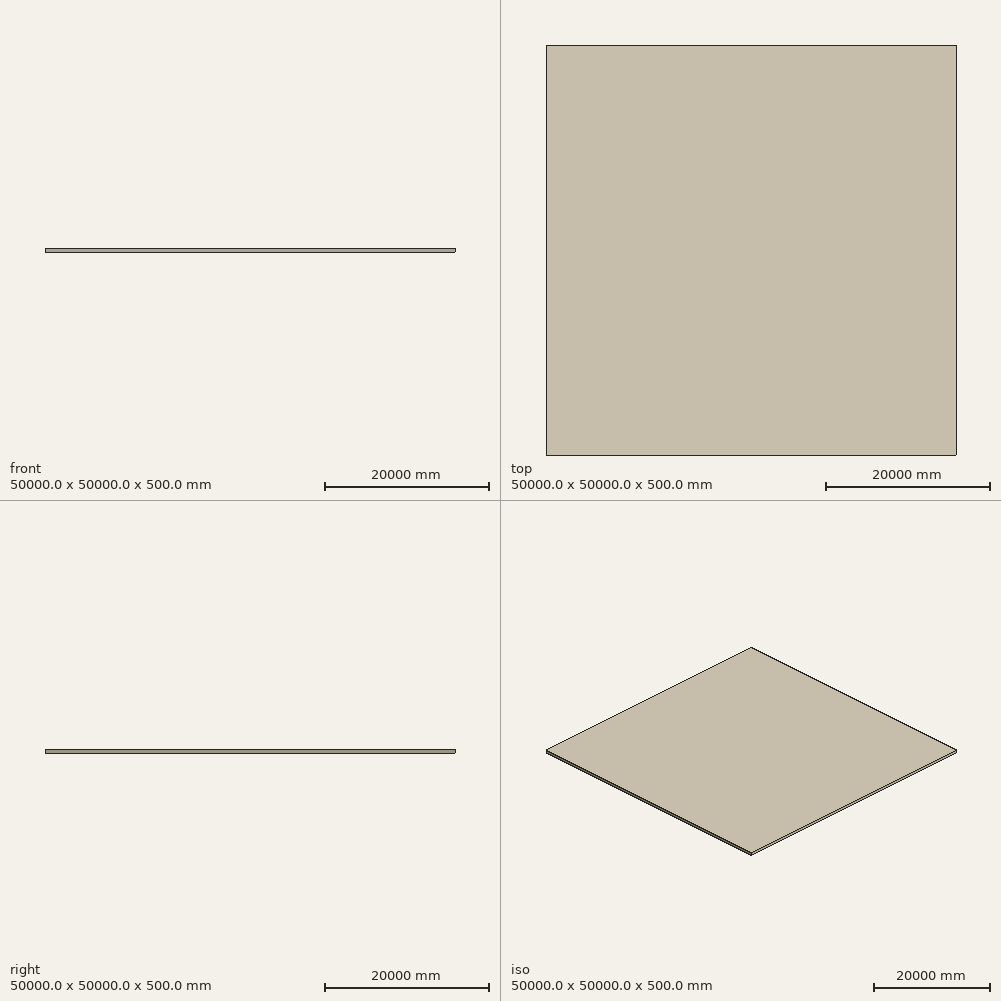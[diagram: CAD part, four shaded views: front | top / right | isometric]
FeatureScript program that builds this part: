
annotation { "Feature Type Name" : "Feature", "Feature Type Description" : "" }
export const myFeature = defineFeature(function(context is Context, id is Id, definition is map)
    precondition{}
    {
        {
            var Q0;
            Q0=qCreatedBy(makeId("Top.planeOp"),FACE);
            var sketch = newSketch(context, id + "F0", { "sketchPlane" : qUnion([Q0])});
            skLineSegment(sketch, "E0.bottom", {"start": v(-25000, 25000) * mm, "end": v(25000, 25000) * mm});
            skLineSegment(sketch, "E0.top", {"start": v(-25000, -25000) * mm, "end": v(25000, -25000) * mm});
            skLineSegment(sketch, "E0.left", {"start": v(-25000, 25000) * mm, "end": v(-25000, -25000) * mm});
            skLineSegment(sketch, "E0.right", {"start": v(25000, 25000) * mm, "end": v(25000, -25000) * mm});
            skLineSegment(sketch, "E1", {"start": v(-25000, 25000) * mm, "end": v(25000, -25000) * mm, "construction": true});
            skSolve(sketch);
        }
        {
            var Q0;
            Q0 = qSketchRegion(id + "F0", true);
            extrude(context, id + "F1", {"entities" : qUnion([Q0]), "oppositeDirection" : true, "depth" : 500 * mm});
        }
    });
